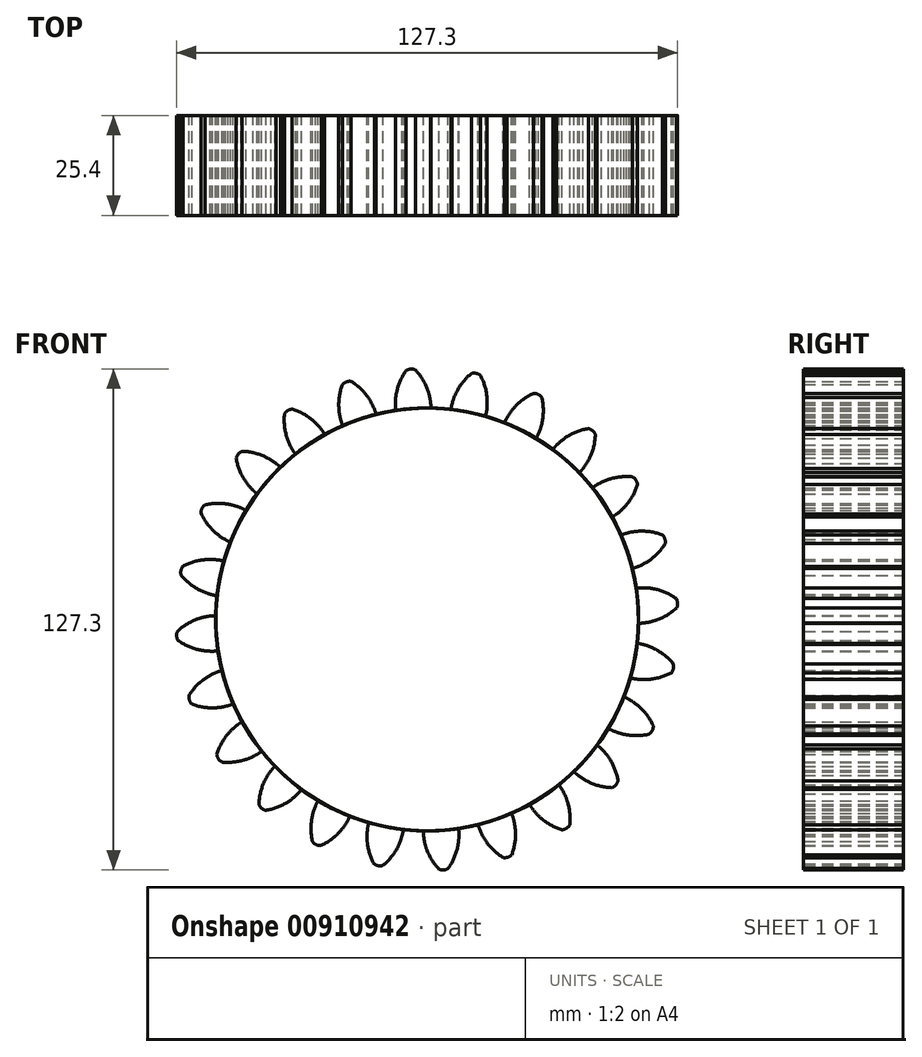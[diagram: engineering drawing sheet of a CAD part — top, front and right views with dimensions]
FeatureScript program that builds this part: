
annotation { "Feature Type Name" : "Feature", "Feature Type Description" : "" }
export const myFeature = defineFeature(function(context is Context, id is Id, definition is map)
    precondition{}
    {
        {
            var Q0;
            Q0=qCreatedBy(makeId("Front.planeOp"),FACE);
            var sketch = newSketch(context, id + "F0", { "sketchPlane" : qUnion([Q0])});
            skCircle(sketch, "E0", {"center": v(0, 0) * mm, "radius": 53.72 * mm});
            skCircle(sketch, "E1", {"center": v(0, 0) * mm, "radius": 58.67 * mm, "construction": true});
            skCircle(sketch, "E2", {"center": v(0, 0) * mm, "radius": 63.5 * mm, "construction": true});
            skLineSegment(sketch, "E3", {"start": v(0, 0) * mm, "end": v(0, 81.47) * mm, "construction": true});
            skLineSegment(sketch, "E4", {"start": v(0, 0) * mm, "end": v(-5.49, 83.74) * mm, "construction": true});
            skLineSegment(sketch, "E5", {"start": v(0, 58.67) * mm, "end": v(-77.65, 58.67) * mm, "construction": true});
            skLineSegment(sketch, "E6", {"start": v(0, 58.67) * mm, "end": v(-71.71, 32.57) * mm, "construction": true});
            skCircle(sketch, "E7", {"center": v(0, 0) * mm, "radius": 55.14 * mm, "construction": true});
            skCircle(sketch, "E8", {"center": v(0, 58.67) * mm, "radius": 14.6 * mm, "construction": true});
            skCircle(sketch, "E9", {"center": v(-13.63, 53.42) * mm, "radius": 14.6 * mm, "construction": true});
            skArc(sketch, "E10", {"start": v(0, 58.67) * mm, "mid": v(-1.26, 61.2) * mm, "end": v(-2.99, 63.43) * mm});
            skArc(sketch, "E11", {"start": v(0.88, 55.13) * mm, "mid": v(0.55, 56.93) * mm, "end": v(0, 58.67) * mm});
            skArc(sketch, "E12", {"start": v(0.97, 53.71) * mm, "mid": v(0.95, 54.42) * mm, "end": v(0.88, 55.13) * mm});
            skArc(sketch, "E13.MirrorCS", {"start": v(-7.66, 58.17) * mm, "mid": v(-6.73, 60.84) * mm, "end": v(-5.32, 63.28) * mm});
            skArc(sketch, "E14.MirrorCS", {"start": v(-7.98, 53.13) * mm, "mid": v(-8.04, 53.83) * mm, "end": v(-8.06, 54.54) * mm});
            skArc(sketch, "E15.MirrorCS", {"start": v(-8.06, 54.54) * mm, "mid": v(-7.98, 56.37) * mm, "end": v(-7.66, 58.17) * mm});
            skArc(sketch, "E16", {"start": v(-2.99, 63.43) * mm, "mid": v(-4.17, 63.64) * mm, "end": v(-5.32, 63.28) * mm});
            skSolve(sketch);
        }
        {
            var Q0;
            {var subQ0=sQuery(id+"F0.wireOp",EDGE,"E0");var subQ1=makeQuery(id+"F0.imprint","INTERSECT",VERTEX,{"derivedFrom":[subQ0,sQuery(id+"F0.wireOp",EDGE,"E12")]});Q0=makeQuery(id+"F0.imprint","IMPRINT",FACE,{"disambiguationData":[TD([[makeQuery(id+"F0.imprint","IMPRINT",EDGE,{"disambiguationData":[TD([[subQ1,-1.0]])],"derivedFrom":subQ0}),1.0]])]});}
            var Q1;
            Q1=makeQuery(id+"F0.imprint","IMPRINT",FACE,{"disambiguationData":[TD([[makeQuery(id+"F0.imprint","IMPRINT",EDGE,{"derivedFrom":sQuery(id+"F0.wireOp",EDGE,"E10")}),1.0]])]});
            extrude(context, id + "F1", {"entities" : qUnion([Q0, Q1]), "depth" : 25.4 * mm, "offsetDistance" : 25.4 * mm});
        }
        {
            var Q0;
            Q0=makeQuery(id+"F1.opExtrude","SWEPT_BODY",BODY,{"disambiguationData":[OSD([sQuery(id+"F0.wireOp",EDGE,"E0"),sQuery(id+"F0.wireOp",EDGE,"E10"),sQuery(id+"F0.wireOp",EDGE,"E11"),sQuery(id+"F0.wireOp",EDGE,"E12"),sQuery(id+"F0.wireOp",EDGE,"E13.MirrorCS"),sQuery(id+"F0.wireOp",EDGE,"E14.MirrorCS"),sQuery(id+"F0.wireOp",EDGE,"E15.MirrorCS"),sQuery(id+"F0.wireOp",EDGE,"E16")])]});
            var Q1;
            Q1=makeQuery(id+"F1.opExtrude","SWEPT_FACE",FACE,{"disambiguationData":[OSD([sQuery(id+"F0.wireOp",EDGE,"E0")])]});
            circularPattern(context, id + "F2", {"entities" : qUnion([Q0]), "axis" : qUnion([Q1]), "angle" : 360 * degree, "instanceCount" : 24, "equalSpace" : true});
        }
    });
